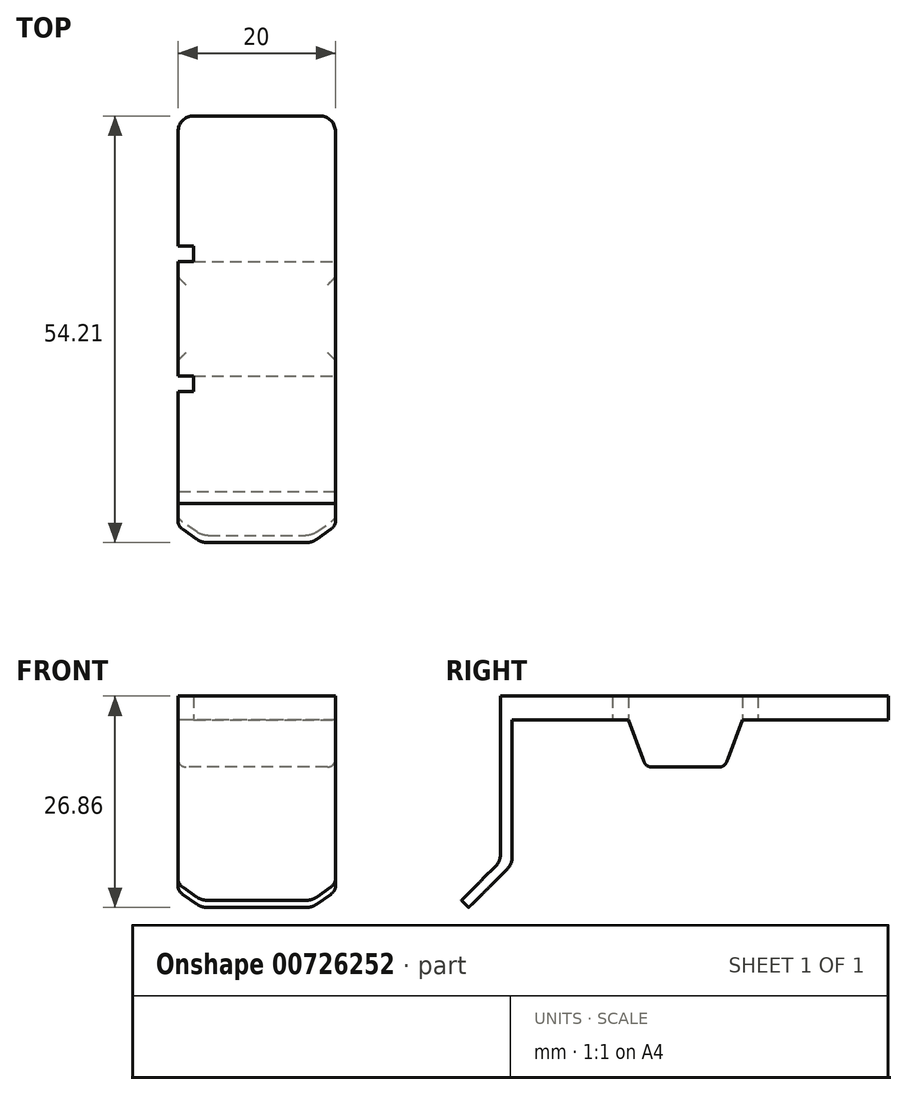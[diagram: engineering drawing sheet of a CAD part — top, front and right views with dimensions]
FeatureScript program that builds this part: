
annotation { "Feature Type Name" : "Feature", "Feature Type Description" : "" }
export const myFeature = defineFeature(function(context is Context, id is Id, definition is map)
    precondition{}
    {
        {
            var Q0;
            Q0=qCreatedBy(makeId("Top.planeOp"),FACE);
            var sketch = newSketch(context, id + "F0", { "sketchPlane" : qUnion([Q0])});
            skLineSegment(sketch, "E0.bottom", {"start": v(10, 23.88) * mm, "end": v(-10, 23.88) * mm});
            skLineSegment(sketch, "E0.top", {"start": v(10, -23.88) * mm, "end": v(-10, -23.88) * mm});
            skLineSegment(sketch, "E0.left", {"start": v(10, 23.88) * mm, "end": v(10, -23.88) * mm});
            skLineSegment(sketch, "E0.right", {"start": v(-10, 23.88) * mm, "end": v(-10, -23.88) * mm});
            skPoint(sketch, "E0.middle", {"position": v(0, 0) * mm});
            skSolve(sketch);
        }
        {
            var Q0;
            Q0=qSketchRegion(id+"F0",true);
            extrude(context, id + "F1", {"entities" : qUnion([Q0]), "depth" : 3 * mm, "offsetDistance" : 25 * mm});
        }
        {
            var Q0;
            Q0=makeQuery(id+"F1.opExtrude","SWEPT_FACE",FACE,{"disambiguationData":[OSD([sQuery(id+"F0.wireOp",EDGE,"E0.top")])]});
            cPlane(context, id + "F2", {"entities" : qUnion([Q0]), "cplaneType" : CPlaneType.OFFSET, "offset" : 0 * mm, "width" : 150 * mm, "height" : 150 * mm});
        }
        {
            var Q0;
            Q0=qCreatedBy(id+"F2.planeOp",FACE);
            var sketch = newSketch(context, id + "F3", { "sketchPlane" : qUnion([Q0])});
            skLineSegment(sketch, "E1.bottom", {"start": v(-10, 3) * mm, "end": v(10, 3) * mm});
            skLineSegment(sketch, "E1.top", {"start": v(-10, -20) * mm, "end": v(10, -20) * mm});
            skLineSegment(sketch, "E1.left", {"start": v(-10, 3) * mm, "end": v(-10, -20) * mm});
            skLineSegment(sketch, "E1.right", {"start": v(10, 3) * mm, "end": v(10, -20) * mm});
            skSolve(sketch);
        }
        {
            var Q0;
            Q0=qSketchRegion(id+"F3",true);
            extrude(context, id + "F4", {"entities" : qUnion([Q0]), "operationType" : NewBodyOperationType.ADD, "depth" : 1.5 * mm, "offsetDistance" : 25 * mm});
        }
        {
            var Q0;
            Q0=makeQuery(id+"F4.opExtrude","CAP_EDGE",EDGE,{"disambiguationData":[OSD([sQuery(id+"F3.wireOp",EDGE,"E1.top")])],"isStart":false});
            chamfer(context, id + "F5", {"entities" : qUnion([Q0]), "chamferType" : ChamferType.OFFSET_ANGLE, "width" : 2 * mm, "oppositeDirection" : false, "angle" : 45 * degree, "tangentPropagation" : true});
        }
        {
            var Q0;
            Q0=makeQuery(id+"F5.opChamfer","BLEND_FACE",FACE,{"disambiguationData":[OSD([sQuery(id+"F3.wireOp",EDGE,"E1.top")])]});
            var sketch = newSketch(context, id + "F6", { "sketchPlane" : qUnion([Q0])});
            skLineSegment(sketch, "E2.bottom", {"start": v(-10, 3.1) * mm, "end": v(10, 3.1) * mm});
            skLineSegment(sketch, "E2.top", {"start": v(-10, 5.22) * mm, "end": v(10, 5.22) * mm});
            skLineSegment(sketch, "E2.left", {"start": v(-10, 3.1) * mm, "end": v(-10, 5.22) * mm});
            skLineSegment(sketch, "E2.right", {"start": v(10, 3.1) * mm, "end": v(10, 5.22) * mm});
            skSolve(sketch);
        }
        {
            var Q0;
            Q0=qSketchRegion(id+"F6",true);
            extrude(context, id + "F7", {"entities" : qUnion([Q0]), "operationType" : NewBodyOperationType.ADD, "depth" : 7 * mm, "offsetDistance" : 25 * mm});
        }
        {
            var Q0;
            Q0=makeQuery(id+"F7.opExtrude","SWEPT_FACE",FACE,{"disambiguationData":[OSD([sQuery(id+"F6.wireOp",EDGE,"E2.bottom")])]});
            var sketch = newSketch(context, id + "F8", { "sketchPlane" : qUnion([Q0])});
            skLineSegment(sketch, "E3.bottom", {"start": v(11.78, -24.05) * mm, "end": v(-11.8, -24.05) * mm});
            skLineSegment(sketch, "E3.top", {"start": v(11.78, -42.1) * mm, "end": v(-11.8, -42.1) * mm});
            skLineSegment(sketch, "E3.left", {"start": v(11.78, -24.05) * mm, "end": v(11.78, -42.1) * mm});
            skLineSegment(sketch, "E3.right", {"start": v(-11.8, -24.05) * mm, "end": v(-11.8, -42.1) * mm});
            skSolve(sketch);
        }
        {
            var Q0;
            Q0 = qSketchRegion(id + "F8", true);
            extrude(context, id + "F9", {"entities" : qUnion([Q0]), "operationType" : NewBodyOperationType.REMOVE, "oppositeDirection" : true, "depth" : .828 * mm, "offsetDistance" : 25 * mm});
        }
        {
            var Q0;
            Q0=makeQuery(id+"F7.opExtrude","CAP_EDGE",EDGE,{"disambiguationData":[OSD([sQuery(id+"F6.wireOp",EDGE,"E2.left")])],"isStart":false});
            var Q1;
            Q1=makeQuery(id+"F7.opExtrude","CAP_EDGE",EDGE,{"disambiguationData":[OSD([sQuery(id+"F6.wireOp",EDGE,"E2.right")])],"isStart":false});
            chamfer(context, id + "F10", {"entities" : qUnion([Q0, Q1]), "width" : 3 * mm, "tangentPropagation" : true});
        }
        {
            var Q0;
            Q0=makeQuery(id+"F1.opExtrude","CAP_EDGE",EDGE,{"disambiguationData":[OSD([sQuery(id+"F0.wireOp",EDGE,"E0.top")])],"isStart":true});
            var Q1;
            Q1=makeQuery(id+"F7.opExtrude","CAP_EDGE",EDGE,{"disambiguationData":[OSD([sQuery(id+"F6.wireOp",EDGE,"E2.top")])],"isStart":true});
            var Q2;
            Q2=makeQuery(id+"F9.boolean.opBoolean","INTERSECT",EDGE,{"derivedFrom":[makeQuery(id+"F4.opExtrude","CAP_FACE",FACE,{"disambiguationData":[OSD([sQuery(id+"F3.wireOp",EDGE,"E1.bottom"),sQuery(id+"F3.wireOp",EDGE,"E1.top"),sQuery(id+"F3.wireOp",EDGE,"E1.left"),sQuery(id+"F3.wireOp",EDGE,"E1.right")])],"isStart":true}),makeQuery(id+"F9.opExtrude","CAP_FACE",FACE,{"disambiguationData":[OSD([sQuery(id+"F8.wireOp",EDGE,"E3.bottom"),sQuery(id+"F8.wireOp",EDGE,"E3.top"),sQuery(id+"F8.wireOp",EDGE,"E3.left"),sQuery(id+"F8.wireOp",EDGE,"E3.right")])],"isStart":false})]});
            var Q3;
            {var subQ0=sQuery(id+"F6.wireOp",EDGE,"E2.left");Q3=makeQuery(id+"F10.opChamfer","BLEND_EDGE",EDGE,{"blendedFrom":[makeQuery(id+"F7.opExtrude","CAP_EDGE",EDGE,{"disambiguationData":[OSD([subQ0])],"isStart":false}),makeQuery(id+"F7.boolean.opBoolean","MERGE",FACE,{"derivedFrom":[makeQuery(id+"F4.boolean.opBoolean","MERGE",FACE,{"derivedFrom":[makeQuery(id+"F1.opExtrude","SWEPT_FACE",FACE,{"disambiguationData":[OSD([sQuery(id+"F0.wireOp",EDGE,"E0.right")])]}),makeQuery(id+"F4.opExtrude","SWEPT_FACE",FACE,{"disambiguationData":[OSD([sQuery(id+"F3.wireOp",EDGE,"E1.left")])]})]}),makeQuery(id+"F7.opExtrude","SWEPT_FACE",FACE,{"disambiguationData":[OSD([subQ0])]})]})],"blendedInto":[makeQuery(id+"F7.boolean.opBoolean","MERGE",FACE,{"derivedFrom":[makeQuery(id+"F4.boolean.opBoolean","MERGE",FACE,{"derivedFrom":[makeQuery(id+"F1.opExtrude","SWEPT_FACE",FACE,{"disambiguationData":[OSD([sQuery(id+"F0.wireOp",EDGE,"E0.right")])]}),makeQuery(id+"F4.opExtrude","SWEPT_FACE",FACE,{"disambiguationData":[OSD([sQuery(id+"F3.wireOp",EDGE,"E1.left")])]})]}),makeQuery(id+"F7.opExtrude","SWEPT_FACE",FACE,{"disambiguationData":[OSD([subQ0])]})]})]});}
            var Q4;
            {var subQ0=sQuery(id+"F6.wireOp",EDGE,"E2.left");Q4=makeQuery(id+"F10.opChamfer","BLEND_EDGE",EDGE,{"blendedFrom":[makeQuery(id+"F7.opExtrude","CAP_EDGE",EDGE,{"disambiguationData":[OSD([subQ0])],"isStart":false}),makeQuery(id+"F7.opExtrude","CAP_FACE",FACE,{"disambiguationData":[OSD([sQuery(id+"F6.wireOp",EDGE,"E2.bottom"),sQuery(id+"F6.wireOp",EDGE,"E2.top"),subQ0,sQuery(id+"F6.wireOp",EDGE,"E2.right")])],"isStart":false})],"blendedInto":[makeQuery(id+"F7.opExtrude","CAP_FACE",FACE,{"disambiguationData":[OSD([sQuery(id+"F6.wireOp",EDGE,"E2.bottom"),sQuery(id+"F6.wireOp",EDGE,"E2.top"),subQ0,sQuery(id+"F6.wireOp",EDGE,"E2.right")])],"isStart":false})]});}
            var Q5;
            {var subQ0=sQuery(id+"F6.wireOp",EDGE,"E2.right");Q5=makeQuery(id+"F10.opChamfer","BLEND_EDGE",EDGE,{"blendedFrom":[makeQuery(id+"F7.opExtrude","CAP_EDGE",EDGE,{"disambiguationData":[OSD([subQ0])],"isStart":false}),makeQuery(id+"F7.opExtrude","CAP_FACE",FACE,{"disambiguationData":[OSD([sQuery(id+"F6.wireOp",EDGE,"E2.bottom"),sQuery(id+"F6.wireOp",EDGE,"E2.top"),sQuery(id+"F6.wireOp",EDGE,"E2.left"),subQ0])],"isStart":false})],"blendedInto":[makeQuery(id+"F7.opExtrude","CAP_FACE",FACE,{"disambiguationData":[OSD([sQuery(id+"F6.wireOp",EDGE,"E2.bottom"),sQuery(id+"F6.wireOp",EDGE,"E2.top"),sQuery(id+"F6.wireOp",EDGE,"E2.left"),subQ0])],"isStart":false})]});}
            var Q6;
            {var subQ0=sQuery(id+"F6.wireOp",EDGE,"E2.right");Q6=makeQuery(id+"F10.opChamfer","BLEND_EDGE",EDGE,{"blendedFrom":[makeQuery(id+"F7.opExtrude","CAP_EDGE",EDGE,{"disambiguationData":[OSD([subQ0])],"isStart":false}),makeQuery(id+"F7.boolean.opBoolean","MERGE",FACE,{"derivedFrom":[makeQuery(id+"F4.boolean.opBoolean","MERGE",FACE,{"derivedFrom":[makeQuery(id+"F1.opExtrude","SWEPT_FACE",FACE,{"disambiguationData":[OSD([sQuery(id+"F0.wireOp",EDGE,"E0.left")])]}),makeQuery(id+"F4.opExtrude","SWEPT_FACE",FACE,{"disambiguationData":[OSD([sQuery(id+"F3.wireOp",EDGE,"E1.right")])]})]}),makeQuery(id+"F7.opExtrude","SWEPT_FACE",FACE,{"disambiguationData":[OSD([subQ0])]})]})],"blendedInto":[makeQuery(id+"F7.boolean.opBoolean","MERGE",FACE,{"derivedFrom":[makeQuery(id+"F4.boolean.opBoolean","MERGE",FACE,{"derivedFrom":[makeQuery(id+"F1.opExtrude","SWEPT_FACE",FACE,{"disambiguationData":[OSD([sQuery(id+"F0.wireOp",EDGE,"E0.left")])]}),makeQuery(id+"F4.opExtrude","SWEPT_FACE",FACE,{"disambiguationData":[OSD([sQuery(id+"F3.wireOp",EDGE,"E1.right")])]})]}),makeQuery(id+"F7.opExtrude","SWEPT_FACE",FACE,{"disambiguationData":[OSD([subQ0])]})]})]});}
            fillet(context, id + "F11", {"entities" : qUnion([Q0, Q1, Q2, Q3, Q4, Q5, Q6]), "radius" : 2 * mm, "tangentPropagation" : true, "allowEdgeOverflow" : false});
        }
        {
            var Q0;
            Q0=makeQuery(id+"F1.opExtrude","CAP_FACE",FACE,{"disambiguationData":[OSD([sQuery(id+"F0.wireOp",EDGE,"E0.bottom"),sQuery(id+"F0.wireOp",EDGE,"E0.top"),sQuery(id+"F0.wireOp",EDGE,"E0.left"),sQuery(id+"F0.wireOp",EDGE,"E0.right")])],"isStart":true});
            var sketch = newSketch(context, id + "F12", { "sketchPlane" : qUnion([Q0])});
            skLineSegment(sketch, "E4.bottom", {"start": v(10, 9.88) * mm, "end": v(-10, 9.88) * mm});
            skLineSegment(sketch, "E4.top", {"start": v(10, -6.12) * mm, "end": v(-10, -6.12) * mm});
            skLineSegment(sketch, "E4.left", {"start": v(10, 9.88) * mm, "end": v(10, -6.12) * mm});
            skLineSegment(sketch, "E4.right", {"start": v(-10, 9.88) * mm, "end": v(-10, -6.12) * mm});
            skPoint(sketch, "E4.middle", {"position": v(0, 1.88) * mm});
            skSolve(sketch);
        }
        {
            var Q0;
            Q0=qSketchRegion(id+"F12",true);
            extrude(context, id + "F13", {"entities" : qUnion([Q0]), "operationType" : NewBodyOperationType.ADD, "depth" : 6 * mm, "offsetDistance" : 25 * mm});
        }
        {
            var Q0;
            Q0=makeQuery(id+"F13.opExtrude","CAP_EDGE",EDGE,{"disambiguationData":[OSD([sQuery(id+"F12.wireOp",EDGE,"E4.bottom")])],"isStart":false});
            var Q1;
            Q1=makeQuery(id+"F13.opExtrude","CAP_EDGE",EDGE,{"disambiguationData":[OSD([sQuery(id+"F12.wireOp",EDGE,"E4.top")])],"isStart":false});
            chamfer(context, id + "F14", {"entities" : qUnion([Q0, Q1]), "chamferType" : ChamferType.TWO_OFFSETS, "width1" : 3 * mm, "oppositeDirection" : false, "width2" : 8 * mm, "tangentPropagation" : true});
        }
        {
            var Q0;
            Q0=makeQuery(id+"F1.opExtrude","SWEPT_EDGE",EDGE,{"disambiguationData":[OSD([sQuery(id+"F0.wireOp",EDGE,"E0.bottom"),sQuery(id+"F0.wireOp",EDGE,"E0.right")])]});
            var Q1;
            Q1=makeQuery(id+"F1.opExtrude","SWEPT_EDGE",EDGE,{"disambiguationData":[OSD([sQuery(id+"F0.wireOp",EDGE,"E0.bottom"),sQuery(id+"F0.wireOp",EDGE,"E0.left")])]});
            fillet(context, id + "F15", {"entities" : qUnion([Q0, Q1]), "radius" : 2 * mm, "tangentPropagation" : true, "allowEdgeOverflow" : false});
        }
        {
            var Q0;
            Q0=makeQuery(id+"F13.opExtrude","CAP_FACE",FACE,{"disambiguationData":[OSD([sQuery(id+"F12.wireOp",EDGE,"E4.bottom"),sQuery(id+"F12.wireOp",EDGE,"E4.top"),sQuery(id+"F12.wireOp",EDGE,"E4.left"),sQuery(id+"F12.wireOp",EDGE,"E4.right")])],"isStart":false});
            fillet(context, id + "F16", {"entities" : qUnion([Q0]), "radius" : 1 * mm, "tangentPropagation" : true, "allowEdgeOverflow" : false});
        }
        {
            var Q0;
            {var subQ0=sQuery(id+"F0.wireOp",EDGE,"E0.left");var subQ1=sQuery(id+"F0.wireOp",EDGE,"E0.right");var subQ2=sQuery(id+"F0.wireOp",EDGE,"E0.bottom");Q0=makeQuery(id+"F13.boolean.opBoolean","SPLIT",FACE,{"disambiguationData":[TD([makeQuery(id+"F1.opExtrude","SWEPT_FACE",FACE,{"disambiguationData":[OSD([subQ2])]})])],"derivedFrom":makeQuery(id+"F1.opExtrude","CAP_FACE",FACE,{"disambiguationData":[OSD([subQ2,sQuery(id+"F0.wireOp",EDGE,"E0.top"),subQ0,subQ1])],"isStart":true})});}
            var sketch = newSketch(context, id + "F17", { "sketchPlane" : qUnion([Q0])});
            skLineSegment(sketch, "E5.bottom", {"start": v(-10, -5.37) * mm, "end": v(-8, -5.37) * mm});
            skLineSegment(sketch, "E5.top", {"start": v(-10, -7.37) * mm, "end": v(-8, -7.37) * mm});
            skLineSegment(sketch, "E5.left", {"start": v(-10, -5.37) * mm, "end": v(-10, -7.37) * mm});
            skLineSegment(sketch, "E5.right", {"start": v(-8, -5.37) * mm, "end": v(-8, -7.37) * mm});
            skPoint(sketch, "E6.firstSnap0", {"position": v(-8, -6.37) * mm});
            skLineSegment(sketch, "E6.bottom", {"start": v(-8, 9.13) * mm, "end": v(-10, 9.13) * mm});
            skLineSegment(sketch, "E6.top", {"start": v(-8, 11.13) * mm, "end": v(-10, 11.13) * mm});
            skLineSegment(sketch, "E6.left", {"start": v(-8, 9.13) * mm, "end": v(-8, 11.13) * mm});
            skLineSegment(sketch, "E6.right", {"start": v(-10, 9.13) * mm, "end": v(-10, 11.13) * mm});
            skSolve(sketch);
        }
        {
            var Q0;
            Q0 = qSketchRegion(id + "F17", true);
            var Q1;
            Q1=makeQuery(id+"F4.boolean.opBoolean","MERGE",FACE,{"derivedFrom":[makeQuery(id+"F1.opExtrude","CAP_FACE",FACE,{"disambiguationData":[OSD([sQuery(id+"F0.wireOp",EDGE,"E0.bottom"),sQuery(id+"F0.wireOp",EDGE,"E0.top"),sQuery(id+"F0.wireOp",EDGE,"E0.left"),sQuery(id+"F0.wireOp",EDGE,"E0.right")])],"isStart":false}),makeQuery(id+"F4.opExtrude","SWEPT_FACE",FACE,{"disambiguationData":[OSD([sQuery(id+"F3.wireOp",EDGE,"E1.bottom")])]})]});
            extrude(context, id + "F18", {"entities" : qUnion([Q0]), "operationType" : NewBodyOperationType.REMOVE, "endBound" : BoundingType.UP_TO_SURFACE, "oppositeDirection" : true, "depth" : 25 * mm, "endBoundEntityFace" : qUnion([Q1]), "offsetDistance" : 25 * mm});
        }
    });
